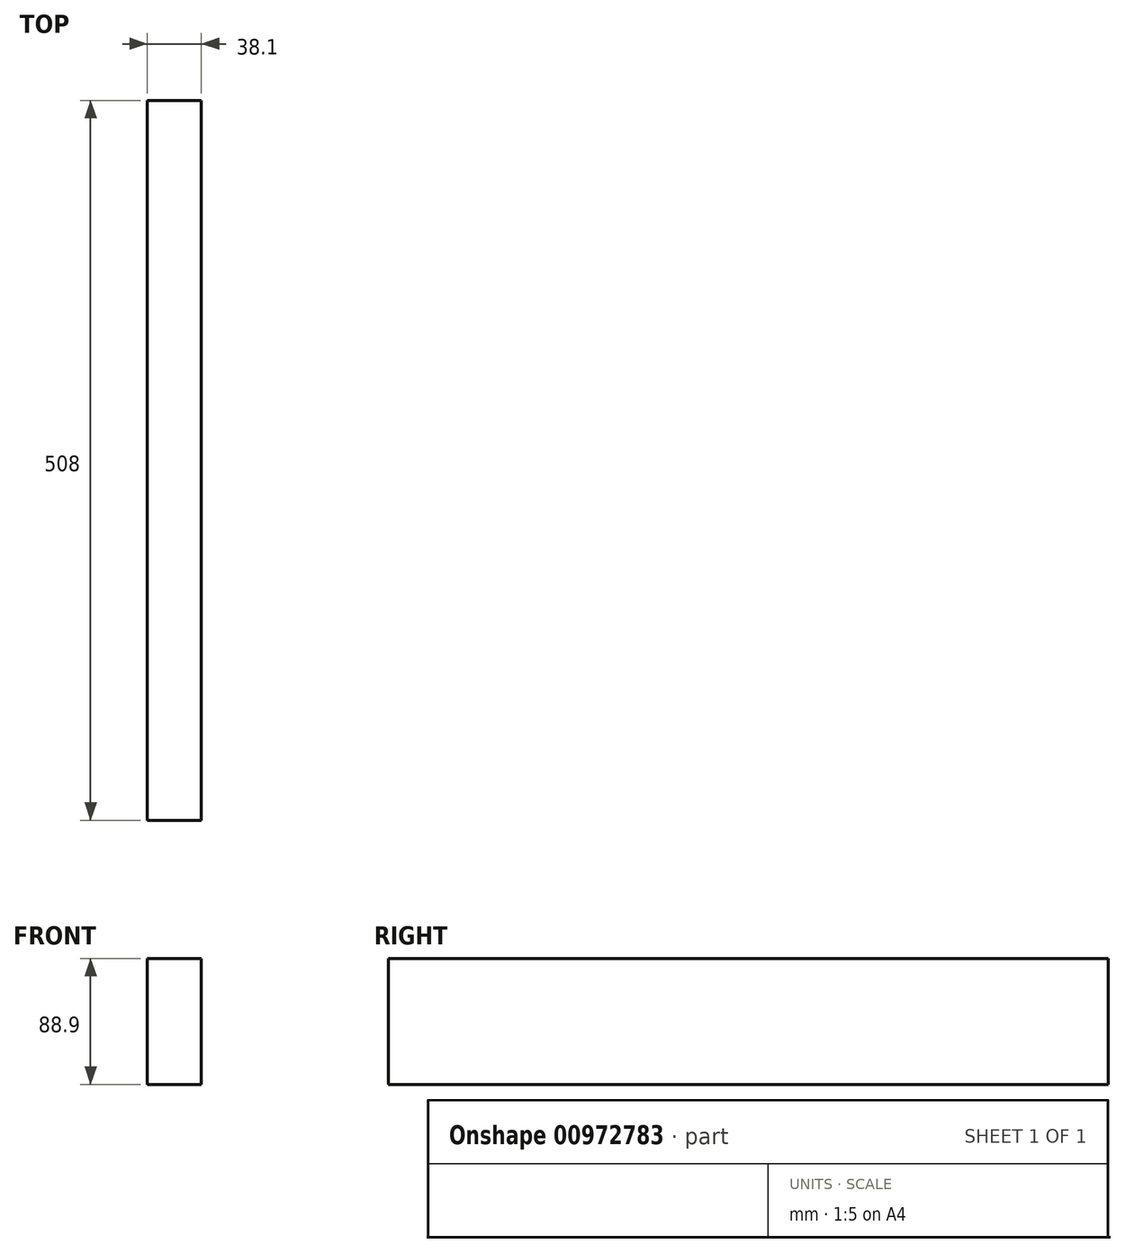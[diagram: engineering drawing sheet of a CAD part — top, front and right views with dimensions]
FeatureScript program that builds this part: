
annotation { "Feature Type Name" : "Feature", "Feature Type Description" : "" }
export const myFeature = defineFeature(function(context is Context, id is Id, definition is map)
    precondition{}
    {
        {
            var Q0;
            Q0=qCreatedBy(makeId("Front.planeOp"),FACE);
            var sketch = newSketch(context, id + "F0", { "sketchPlane" : qUnion([Q0])});
            skLineSegment(sketch, "E0.bottom", {"start": v(0, 0) * mm, "end": v(38.1, 0) * mm});
            skLineSegment(sketch, "E0.top", {"start": v(0, 88.9) * mm, "end": v(38.1, 88.9) * mm});
            skLineSegment(sketch, "E0.left", {"start": v(0, 0) * mm, "end": v(0, 88.9) * mm});
            skLineSegment(sketch, "E0.right", {"start": v(38.1, 0) * mm, "end": v(38.1, 88.9) * mm});
            skSolve(sketch);
        }
        {
            var Q0;
            Q0=makeQuery(id+"F0.imprint","IMPRINT",FACE,{"disambiguationData":[TD([[makeQuery(id+"F0.imprint","IMPRINT",EDGE,{"derivedFrom":sQuery(id+"F0.wireOp",EDGE,"E0.bottom")}),1.0]])]});
            extrude(context, id + "F1", {"entities" : qUnion([Q0]), "depth" : 508 * mm, "offsetDistance" : 25.4 * mm});
        }
    });
